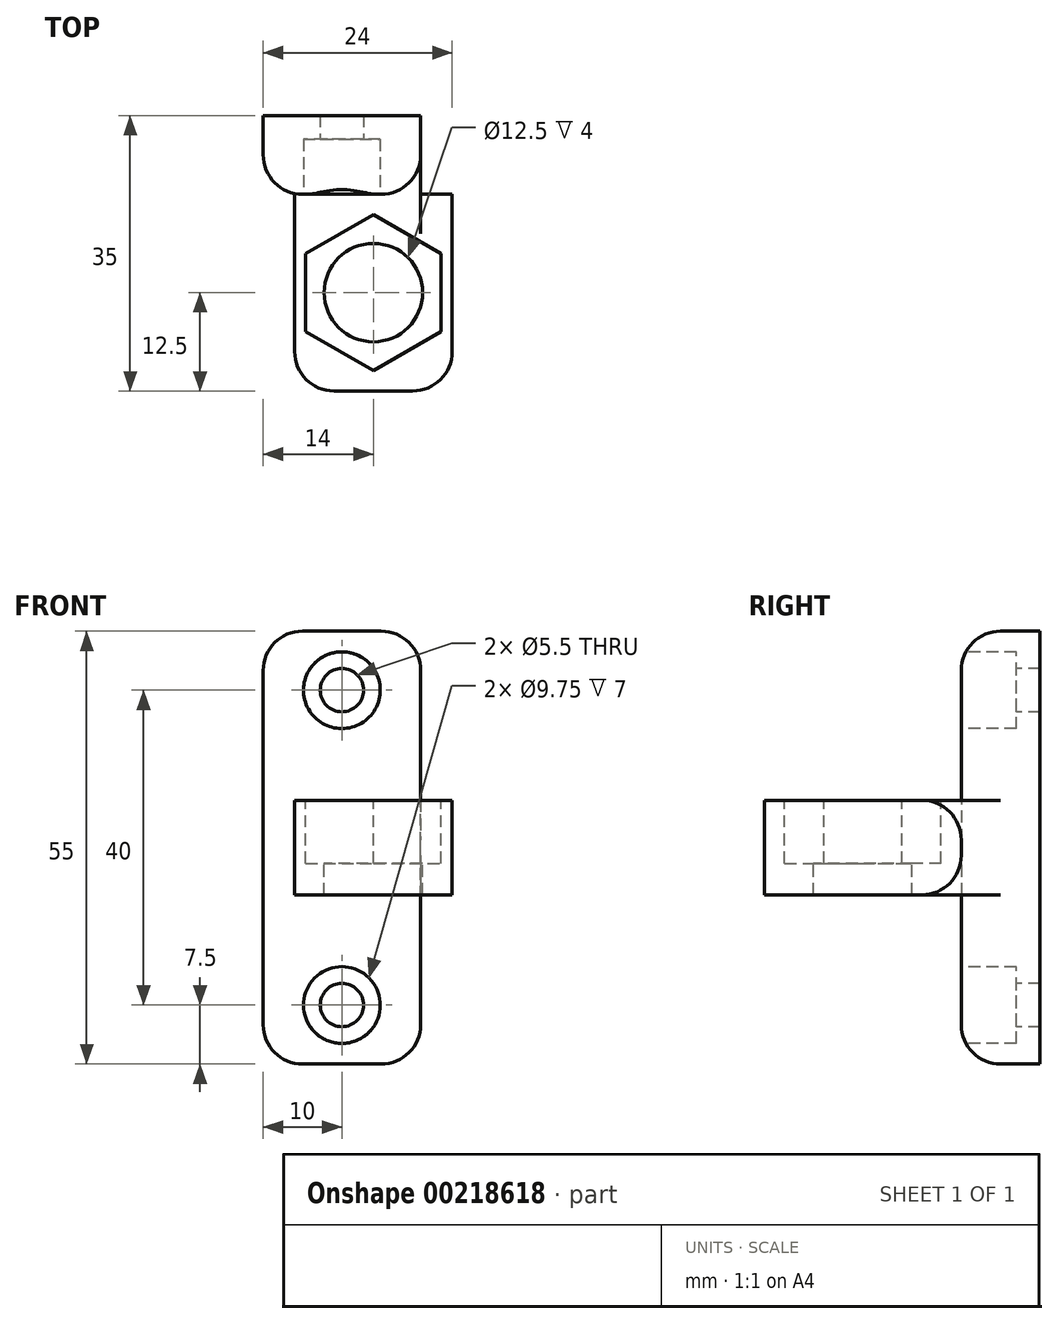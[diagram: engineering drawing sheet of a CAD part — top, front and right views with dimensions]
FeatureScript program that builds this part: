
annotation { "Feature Type Name" : "Feature", "Feature Type Description" : "" }
export const myFeature = defineFeature(function(context is Context, id is Id, definition is map)
    precondition{}
    {
        {
            var Q0;
            Q0=qCreatedBy(makeId("Front.planeOp"),FACE);
            var sketch = newSketch(context, id + "F0", { "sketchPlane" : qUnion([Q0])});
            skLineSegment(sketch, "E0.bottom", {"start": v(0, 0) * mm, "end": v(20, 0) * mm});
            skLineSegment(sketch, "E0.top", {"start": v(0, 55) * mm, "end": v(20, 55) * mm});
            skLineSegment(sketch, "E0.left", {"start": v(0, 0) * mm, "end": v(0, 55) * mm});
            skLineSegment(sketch, "E0.right", {"start": v(20, 0) * mm, "end": v(20, 55) * mm});
            skSolve(sketch);
        }
        {
            var Q0;
            Q0 = qSketchRegion(id + "F0", true);
            extrude(context, id + "F1", {"entities" : qUnion([Q0]), "depth" : 10 * mm, "offsetDistance" : 25 * mm});
        }
        {
            var Q0;
            Q0=makeQuery(id+"F1.opExtrude","CAP_FACE",FACE,{"disambiguationData":[OSD([sQuery(id+"F0.wireOp",EDGE,"E0.bottom"),sQuery(id+"F0.wireOp",EDGE,"E0.top"),sQuery(id+"F0.wireOp",EDGE,"E0.left"),sQuery(id+"F0.wireOp",EDGE,"E0.right")])],"isStart":false});
            var sketch = newSketch(context, id + "F2", { "sketchPlane" : qUnion([Q0])});
            skCircle(sketch, "E1", {"center": v(10, 7.5) * mm, "radius": 2.75 * mm});
            skLineSegment(sketch, "E2", {"start": v(0, 27.5) * mm, "end": v(20, 27.5) * mm, "construction": true});
            skCircle(sketch, "E3.MirrorC", {"center": v(10, 47.5) * mm, "radius": 2.75 * mm});
            skSolve(sketch);
        }
        {
            var Q0;
            Q0 = qSketchRegion(id + "F2", true);
            extrude(context, id + "F3", {"entities" : qUnion([Q0]), "operationType" : NewBodyOperationType.REMOVE, "endBound" : BoundingType.THROUGH_ALL, "oppositeDirection" : true, "depth" : 25 * mm, "offsetDistance" : 25 * mm});
        }
        {
            var Q0;
            Q0=makeQuery(id+"F1.opExtrude","CAP_FACE",FACE,{"disambiguationData":[OSD([sQuery(id+"F0.wireOp",EDGE,"E0.bottom"),sQuery(id+"F0.wireOp",EDGE,"E0.top"),sQuery(id+"F0.wireOp",EDGE,"E0.left"),sQuery(id+"F0.wireOp",EDGE,"E0.right")])],"isStart":false});
            var sketch = newSketch(context, id + "F4", { "sketchPlane" : qUnion([Q0])});
            skLineSegment(sketch, "E4.bottom", {"start": v(4, 21.5) * mm, "end": v(24, 21.5) * mm});
            skLineSegment(sketch, "E4.top", {"start": v(4, 33.5) * mm, "end": v(24, 33.5) * mm});
            skLineSegment(sketch, "E4.left", {"start": v(4, 21.5) * mm, "end": v(4, 33.5) * mm});
            skLineSegment(sketch, "E4.right", {"start": v(24, 21.5) * mm, "end": v(24, 33.5) * mm});
            skPoint(sketch, "E5", {"position": v(4, 27.5) * mm});
            skSolve(sketch);
        }
        {
            var Q0;
            Q0 = qSketchRegion(id + "F4", true);
            extrude(context, id + "F5", {"entities" : qUnion([Q0]), "operationType" : NewBodyOperationType.ADD, "depth" : 25 * mm, "offsetDistance" : 25 * mm});
        }
        {
            var Q0;
            Q0=makeQuery(id+"F5.opExtrude","SWEPT_FACE",FACE,{"disambiguationData":[OSD([sQuery(id+"F4.wireOp",EDGE,"E4.top")])]});
            var sketch = newSketch(context, id + "F6", { "sketchPlane" : qUnion([Q0])});
            skCircle(sketch, "E6.cCircle", {"center": v(14, -22.5) * mm, "radius": 8.6 * mm, "construction": true});
            skLineSegment(sketch, "E6.0", {"start": v(14, -12.57) * mm, "end": v(22.6, -17.53) * mm});
            skLineSegment(sketch, "E6.1", {"start": v(22.6, -17.53) * mm, "end": v(22.6, -27.47) * mm});
            skLineSegment(sketch, "E6.2", {"start": v(22.6, -27.47) * mm, "end": v(14, -32.43) * mm});
            skLineSegment(sketch, "E6.3", {"start": v(14, -32.43) * mm, "end": v(5.4, -27.47) * mm});
            skLineSegment(sketch, "E6.4", {"start": v(5.4, -27.47) * mm, "end": v(5.4, -17.53) * mm});
            skLineSegment(sketch, "E6.5", {"start": v(5.4, -17.53) * mm, "end": v(14, -12.57) * mm});
            skPoint(sketch, "E6.0.midPoint", {"position": v(18.3, -15.05) * mm});
            skSolve(sketch);
        }
        {
            var Q0;
            Q0 = qSketchRegion(id + "F6", true);
            extrude(context, id + "F7", {"entities" : qUnion([Q0]), "operationType" : NewBodyOperationType.REMOVE, "oppositeDirection" : true, "depth" : 8 * mm, "offsetDistance" : 25 * mm});
        }
        {
            var Q0;
            Q0=makeQuery(id+"F7.boolean.opBoolean","COPY",FACE,{"derivedFrom":makeQuery(id+"F7.opExtrude","CAP_FACE",FACE,{"disambiguationData":[OSD([sQuery(id+"F6.wireOp",EDGE,"E6.0"),sQuery(id+"F6.wireOp",EDGE,"E6.1"),sQuery(id+"F6.wireOp",EDGE,"E6.2"),sQuery(id+"F6.wireOp",EDGE,"E6.3"),sQuery(id+"F6.wireOp",EDGE,"E6.4"),sQuery(id+"F6.wireOp",EDGE,"E6.5")])],"isStart":false})});
            var sketch = newSketch(context, id + "F8", { "sketchPlane" : qUnion([Q0])});
            skCircle(sketch, "E7", {"center": v(14, -22.5) * mm, "radius": 6.25 * mm});
            skPoint(sketch, "E7.centerSnap0", {"position": v(5.4, -22.5) * mm});
            skSolve(sketch);
        }
        {
            var Q0;
            Q0 = qSketchRegion(id + "F8", true);
            extrude(context, id + "F9", {"entities" : qUnion([Q0]), "operationType" : NewBodyOperationType.REMOVE, "endBound" : BoundingType.THROUGH_ALL, "oppositeDirection" : true, "depth" : 25 * mm, "offsetDistance" : 25 * mm});
        }
        {
            var Q0;
            {var subQ0=sQuery(id+"F0.wireOp",EDGE,"E0.right");var subQ1=sQuery(id+"F0.wireOp",EDGE,"E0.left");var subQ2=sQuery(id+"F0.wireOp",EDGE,"E0.top");Q0=makeQuery(id+"F5.boolean.opBoolean","SPLIT",FACE,{"disambiguationData":[TD([makeQuery(id+"F1.opExtrude","SWEPT_FACE",FACE,{"disambiguationData":[OSD([subQ2])]})])],"derivedFrom":makeQuery(id+"F1.opExtrude","CAP_FACE",FACE,{"disambiguationData":[OSD([sQuery(id+"F0.wireOp",EDGE,"E0.bottom"),subQ2,subQ1,subQ0])],"isStart":false})});}
            var sketch = newSketch(context, id + "F10", { "sketchPlane" : qUnion([Q0])});
            skCircle(sketch, "E8", {"center": v(10, 47.5) * mm, "radius": 4.88 * mm});
            skCircle(sketch, "E9", {"center": v(10, 7.5) * mm, "radius": 4.88 * mm});
            skSolve(sketch);
        }
        {
            var Q0;
            Q0 = qSketchRegion(id + "F10", true);
            extrude(context, id + "F11", {"entities" : qUnion([Q0]), "operationType" : NewBodyOperationType.REMOVE, "oppositeDirection" : true, "depth" : 7 * mm, "offsetDistance" : 25 * mm});
        }
        {
            var Q0;
            Q0=makeQuery(id+"F5.opExtrude","CAP_EDGE",EDGE,{"disambiguationData":[OSD([sQuery(id+"F4.wireOp",EDGE,"gFwteAez-JEg4-XMt5-jBkt-w07Q3YrJvI1K.bottom")])],"isStart":true});
            var Q1;
            Q1=makeQuery(id+"F5.opExtrude","CAP_EDGE",EDGE,{"disambiguationData":[OSD([sQuery(id+"F4.wireOp",EDGE,"gFwteAez-JEg4-XMt5-jBkt-w07Q3YrJvI1K.top")])],"isStart":true});
            var Q2;
            Q2=makeQuery(id+"F1.opExtrude","SWEPT_EDGE",EDGE,{"disambiguationData":[OSD([sQuery(id+"F0.wireOp",EDGE,"E0.top"),sQuery(id+"F0.wireOp",EDGE,"E0.left")])]});
            var Q3;
            Q3=makeQuery(id+"F1.opExtrude","SWEPT_EDGE",EDGE,{"disambiguationData":[OSD([sQuery(id+"F0.wireOp",EDGE,"E0.top"),sQuery(id+"F0.wireOp",EDGE,"E0.right")])]});
            var Q4;
            Q4=makeQuery(id+"F1.opExtrude","SWEPT_EDGE",EDGE,{"disambiguationData":[OSD([sQuery(id+"F0.wireOp",EDGE,"E0.bottom"),sQuery(id+"F0.wireOp",EDGE,"E0.left")])]});
            var Q5;
            Q5=makeQuery(id+"F1.opExtrude","SWEPT_EDGE",EDGE,{"disambiguationData":[OSD([sQuery(id+"F0.wireOp",EDGE,"E0.bottom"),sQuery(id+"F0.wireOp",EDGE,"E0.right")])]});
            var Q6;
            Q6=makeQuery(id+"F5.opExtrude","CAP_EDGE",EDGE,{"disambiguationData":[OSD([sQuery(id+"F4.wireOp",EDGE,"gFwteAez-JEg4-XMt5-jBkt-w07Q3YrJvI1K.right")])],"isStart":false});
            var Q7;
            Q7=makeQuery(id+"F5.opExtrude","CAP_EDGE",EDGE,{"disambiguationData":[OSD([sQuery(id+"F4.wireOp",EDGE,"gFwteAez-JEg4-XMt5-jBkt-w07Q3YrJvI1K.left")])],"isStart":false});
            fillet(context, id + "F12", {"entities" : qUnion([Q0, Q1, Q2, Q3, Q4, Q5, Q6, Q7]), "radius" : 5 * mm, "tangentPropagation" : true, "allowEdgeOverflow" : false});
        }
        {
            var Q0;
            Q0=makeQuery(id+"F5.opExtrude","CAP_EDGE",EDGE,{"disambiguationData":[OSD([sQuery(id+"F4.wireOp",EDGE,"E4.left")])],"isStart":true});
            var Q1;
            {var subQ0=sQuery(id+"F0.wireOp",EDGE,"E0.right");Q1=makeQuery(id+"F5.boolean.opBoolean","SPLIT",EDGE,{"disambiguationData":[topologyDisambiguationEdgeConnected([makeQuery(id+"F1.opExtrude","SWEPT_FACE",FACE,{"disambiguationData":[OSD([subQ0])]}),makeQuery(id+"F5.opExtrude","CAP_FACE",FACE,{"disambiguationData":[OSD([sQuery(id+"F4.wireOp",EDGE,"E4.bottom"),sQuery(id+"F4.wireOp",EDGE,"E4.top"),sQuery(id+"F4.wireOp",EDGE,"E4.left"),sQuery(id+"F4.wireOp",EDGE,"E4.right")])],"isStart":true})])],"derivedFrom":makeQuery(id+"F1.opExtrude","CAP_EDGE",EDGE,{"disambiguationData":[OSD([subQ0])],"isStart":false})});}
            fillet(context, id + "F13", {"entities" : qUnion([Q0, Q1]), "radius" : 5 * mm, "tangentPropagation" : true, "allowEdgeOverflow" : false});
        }
        {
            var Q0;
            {var subQ0=sQuery(id+"F4.wireOp",EDGE,"E4.bottom");Q0=makeQuery(id+"F5.boolean.opBoolean","SPLIT",EDGE,{"disambiguationData":[topologyDisambiguationEdgeConnected([makeQuery(id+"F1.opExtrude","CAP_FACE",FACE,{"disambiguationData":[OSD([sQuery(id+"F0.wireOp",EDGE,"E0.bottom"),sQuery(id+"F0.wireOp",EDGE,"E0.top"),sQuery(id+"F0.wireOp",EDGE,"E0.left"),sQuery(id+"F0.wireOp",EDGE,"E0.right")])],"isStart":false})])],"derivedFrom":makeQuery(id+"F5.opExtrude","CAP_EDGE",EDGE,{"disambiguationData":[OSD([subQ0])],"isStart":true})});}
            var Q1;
            {var subQ0=sQuery(id+"F4.wireOp",EDGE,"E4.top");Q1=makeQuery(id+"F5.boolean.opBoolean","SPLIT",EDGE,{"disambiguationData":[topologyDisambiguationEdgeConnected([makeQuery(id+"F1.opExtrude","CAP_FACE",FACE,{"disambiguationData":[OSD([sQuery(id+"F0.wireOp",EDGE,"E0.bottom"),sQuery(id+"F0.wireOp",EDGE,"E0.top"),sQuery(id+"F0.wireOp",EDGE,"E0.left"),sQuery(id+"F0.wireOp",EDGE,"E0.right")])],"isStart":false})])],"derivedFrom":makeQuery(id+"F5.opExtrude","CAP_EDGE",EDGE,{"disambiguationData":[OSD([subQ0])],"isStart":true})});}
            var Q2;
            {var subQ0=sQuery(id+"F4.wireOp",EDGE,"E4.bottom");var subQ1=sQuery(id+"F0.wireOp",EDGE,"E0.right");Q2=makeQuery(id+"F13.opFillet","TWEAK_EDGE",EDGE,{"derivedFrom":[makeQuery(id+"F5.boolean.opBoolean","TWEAK_VERTEX",VERTEX,{"derivedFrom":[makeQuery(id+"F1.opExtrude","SWEPT_FACE",FACE,{"disambiguationData":[OSD([subQ1])]}),makeQuery(id+"F1.opExtrude","CAP_FACE",FACE,{"disambiguationData":[OSD([sQuery(id+"F0.wireOp",EDGE,"E0.bottom"),sQuery(id+"F0.wireOp",EDGE,"E0.top"),sQuery(id+"F0.wireOp",EDGE,"E0.left"),subQ1])],"isStart":false}),makeQuery(id+"F5.opExtrude","SWEPT_FACE",FACE,{"disambiguationData":[OSD([subQ0])]}),makeQuery(id+"F5.opExtrude","CAP_FACE",FACE,{"disambiguationData":[OSD([subQ0,sQuery(id+"F4.wireOp",EDGE,"E4.top"),sQuery(id+"F4.wireOp",EDGE,"E4.left"),sQuery(id+"F4.wireOp",EDGE,"E4.right")])],"isStart":true})]})]});}
            var Q3;
            {var subQ0=sQuery(id+"F4.wireOp",EDGE,"E4.top");var subQ1=sQuery(id+"F0.wireOp",EDGE,"E0.right");Q3=makeQuery(id+"F13.opFillet","TWEAK_EDGE",EDGE,{"derivedFrom":[makeQuery(id+"F5.boolean.opBoolean","TWEAK_VERTEX",VERTEX,{"derivedFrom":[makeQuery(id+"F1.opExtrude","SWEPT_FACE",FACE,{"disambiguationData":[OSD([subQ1])]}),makeQuery(id+"F1.opExtrude","CAP_FACE",FACE,{"disambiguationData":[OSD([sQuery(id+"F0.wireOp",EDGE,"E0.bottom"),sQuery(id+"F0.wireOp",EDGE,"E0.top"),sQuery(id+"F0.wireOp",EDGE,"E0.left"),subQ1])],"isStart":false}),makeQuery(id+"F5.opExtrude","CAP_FACE",FACE,{"disambiguationData":[OSD([sQuery(id+"F4.wireOp",EDGE,"E4.bottom"),subQ0,sQuery(id+"F4.wireOp",EDGE,"E4.left"),sQuery(id+"F4.wireOp",EDGE,"E4.right")])],"isStart":true}),makeQuery(id+"F5.opExtrude","SWEPT_FACE",FACE,{"disambiguationData":[OSD([subQ0])]})]})]});}
            fillet(context, id + "F14", {"entities" : qUnion([Q0, Q1, Q2, Q3]), "radius" : 5 * mm, "tangentPropagation" : true, "allowEdgeOverflow" : false});
        }
        {
            var Q0;
            {var subQ0=sQuery(id+"F4.wireOp",EDGE,"E4.right");var subQ1=sQuery(id+"F0.wireOp",EDGE,"E0.right");Q0=makeQuery(id+"F13.opFillet","BLEND_EDGE",EDGE,{"blendedFrom":[makeQuery(id+"F5.boolean.opBoolean","SPLIT",EDGE,{"disambiguationData":[topologyDisambiguationEdgeConnected([makeQuery(id+"F1.opExtrude","SWEPT_FACE",FACE,{"disambiguationData":[OSD([subQ1])]}),makeQuery(id+"F5.opExtrude","CAP_FACE",FACE,{"disambiguationData":[OSD([sQuery(id+"F4.wireOp",EDGE,"E4.bottom"),sQuery(id+"F4.wireOp",EDGE,"E4.top"),sQuery(id+"F4.wireOp",EDGE,"E4.left"),subQ0])],"isStart":true})])],"derivedFrom":makeQuery(id+"F1.opExtrude","CAP_EDGE",EDGE,{"disambiguationData":[OSD([subQ1])],"isStart":false})}),makeQuery(id+"F5.opExtrude","SWEPT_FACE",FACE,{"disambiguationData":[OSD([subQ0])]})],"blendedInto":[makeQuery(id+"F5.opExtrude","SWEPT_FACE",FACE,{"disambiguationData":[OSD([subQ0])]})]});}
            var Q1;
            Q1=makeQuery(id+"F5.opExtrude","CAP_EDGE",EDGE,{"disambiguationData":[OSD([sQuery(id+"F4.wireOp",EDGE,"E4.right")])],"isStart":false});
            var Q2;
            Q2=makeQuery(id+"F5.opExtrude","CAP_EDGE",EDGE,{"disambiguationData":[OSD([sQuery(id+"F4.wireOp",EDGE,"E4.left")])],"isStart":false});
            fillet(context, id + "F15", {"entities" : qUnion([Q0, Q1, Q2]), "radius" : 5 * mm, "tangentPropagation" : true, "allowEdgeOverflow" : false});
        }
    });
